# Revit family: Varmax 275-320_4 tomas
name_source: partatom
category: Mechanical Equipment
revit_build: Autodesk Revit 2014 (Build: 20130308_1515(x64)
units: mm (PartAtom-declared; Revit-internal decimal feet)

## types (2) — shared parameters
Alt. conec. = 1672 mm  [stored 5.48556 ft]
Alt. derivación gas = 1413 mm  [stored 4.63583 ft]
Alt. entrada de aire = 1661 mm  [stored 5.44948 ft]
Alt. entrada/salida retorno = 1265 mm  [stored 4.15026 ft]
Altura = 1877 mm  [stored 6.15814 ft]
Ancho = 812 mm  [stored 2.66404 ft]
Assembly Code = D3020100
Conector = 169 mm  [stored 0.554462 ft]
Configuración = 4 tomas
Derivacion de gas = 38 mm
Derivación de vaciado = 25 mm  [stored 0.082021 ft]
Derivación salida / retorno = 51 mm
Empresa creadora del BIM = ACAE
Entrada de aire = 180 mm  [stored 0.590551 ft]
Manufacturer = Atlantic
Mínimo = 45 mm
Peso en vacío = 490 kg
Presión máxima de servicio = 6 bar
Profundidad Total = 1341 mm  [stored 4.39961 ft]
Rendimiento mínimo al 100% de potencia (80/60 ºC) = 97,9%
Rendimiento mínimo al 30% de carga (50/30 ºC) = 108%
Salida de humos = 180 mm  [stored 0.590551 ft]
Tipo de combustible = Gas natural (G20), en opción Gas propano (G31) hasta 320 kW
URL = http://www.ygnis.es
Volumen de agua = 239 L

## per-type parameters (varying)
| type | Caudal de gas a Pn (15 ºC) | Consumo eléctrico máximo | Description | Model | Potencia útil (50/30 ºC) | Salida de humo |
| Varmax 275 - Caldera de pie de condensación a gas 291 kW y 6 bar (4 tomas) | 29,1 m3/h | 238 W | Unidad térmica de condensación para gas natural Ygnis modelo Varmax 275,  potencia útil (50/30 ºC) de 291 kW. Fabricada en acero inoxidable de alta calidad AISI 316 L. Quemador modulante desde el 20% de la potencia. Rendimiento hasta el 108 %. Clase 5 de NOx. Dimensiones (Altura x Ancho x Largo): 1932 x 800 x 1316 mm. Peso en vacío: 490 kg. Presión máxima de servicio: 6 bar. Configuración a 4 tomas.
127 y 478kW. | Varmax 275 | 291 kW | 0 mm  [stored 0 ft] |
| Varmax 320 - Caldera de pie de condensación a gas 338 kW y 6 bar (4 tomas) | 33,86 m3/h | 352 W | Unidad térmica de condensación para gas natural Ygnis modelo Varmax 320,  potencia útil (50/30 ºC) de 338 kW. Fabricada en acero inoxidable de alta calidad AISI 316 L. Quemador modulante desde el 20% de la potencia. Rendimiento hasta el 108 %. Clase 5 de NOx. Dimensiones (Altura x Ancho x Largo): 1932 x 800 x 1316 mm. Peso en vacío: 490 kg. Presión máxima de servicio: 6 bar. Configuración a 4 tomas. | Varmax 320 | 338 kW | 150 mm |

note: [stored X ft] marks values corroborated as IEEE doubles in the binary element streams (Revit-internal decimal feet)

## geometry (parser evidence)
native form markers: Sweep x1
no freeform markers — native parametric forms only
